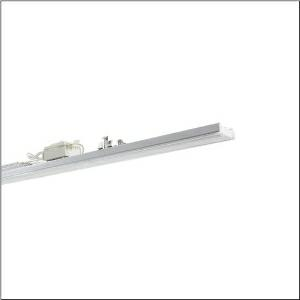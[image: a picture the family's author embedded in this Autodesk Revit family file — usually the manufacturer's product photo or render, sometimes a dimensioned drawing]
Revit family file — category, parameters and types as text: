
# Revit family: licross_21_recessed_mo_52tl14de445g
name_source: partatom
category: Lighting Fixtures
units: mm (PartAtom-declared; Revit-internal decimal feet)

## family parameters
Cut with Voids When Loaded = No
Host = Face
Light Source = No
Part Type = Normal
Room Calculation Point = No
Round Connector Dimension = Use Diameter
Shared = No

## types (1)
- --- (1 x LED, 4730 lm, 29.9 W, 4000K)
    Apparent Load = 30 VA
    CIE Flux Codes = 56 84 97 100 100
    Color Rendering = 80
    Color Temperature = 4000K
    Default Elevation = 1800 mm
    Description = Licross 21 Recessed MO, luminaire insert, of sheet steel, galvanised, coil coated, white, length: 750mm, width: 66mm, height: 67mm, LED rated luminous flux: 4.730lm, light colour: 840, SDCM (Standard Deviation of Colour Matching)MacAdam ≤ 3 SDCM (initial), control gear: DALI 2, with plug, 5-pole, with phase selection, mains connection: 220..240V, AC, 50/60Hz, rated input power: 30W, internal wiring halogen-free, primary light control with lens, of plastic, primary optical cover: cover, of PMMA, light emission: direct distribution, primary light characteristic: asymmetric, protection rating (complete): IP40, insulation class (complete): insulation class I (protective earthing), certification: CE, ENEC, VDE, UKCA, protection symbol: D if used in an environment without relevant dust loads with corresponding accessories, impact resistance: IK06, permissible ambient temperature for indoor applications: -25..+35°C, corresponds to IFS (International Featured Standards) requirements for safety and quality in the food industry, reducing of maximum allowable ambient temperature of 5°C with ceiling mounting, LABS conformity tested according to VDMA 24364:2018-05, The light source and the operating device comply with the requirements of the Ecodesign Regulation (EU) 2019/2020 and are replaceable in accordance with this regulation, packaging unit: 1 piece
    Height = 58 mm
    Lamp = 1 x LED
    Lamp Light Flux = 4730 lm
    Lamp Power = 29.9 W
    Lamp count = 1
    Length = 750 mm
    Luminous efficacy = 158 lm/W
    Manufacturer = Siteco
    ModVariant = No
    Model = 52TL14DE445G
    Mounting Place = Ceiling
    Mounting Type = Pendant
    Number of Poles = 1
    OnlyDefault = Yes
    Power Factor = 1
    Product Name = Licross 21 Recessed MO
    Product group = luminaire insert | ceiling pendant
    ProductGroupID = 901
    Protection Class = Protection class I
    Protection Degree = IP 40
    RLX_Detail_Level = 1
    RLX_Emergency_Light_Flux = 0 lm
    RLX_Emergency_Type = 0
    RLX_Emergency_Type_DB = No
    RlxData = <blob elided: 29285 chars, md5=892036e6>
    Socket = socket
    Standby Power = 0 W
    System Light Flux = 4730 lm
    System Power = 30 W
    Type Comments = factory setting: luminous flux: 100 % | dim-lin: 254 | 390 mA
    Type Image = l_1296930.jpg
    URL = http://relux.com
    VarID = @adj_128051
    Voltage = 0 V
    Weight = 0.00 kg
    Width = 66 mm

## geometry (parser evidence)
native form markers: Blend x4, Sweep x8
no freeform markers — native parametric forms only
